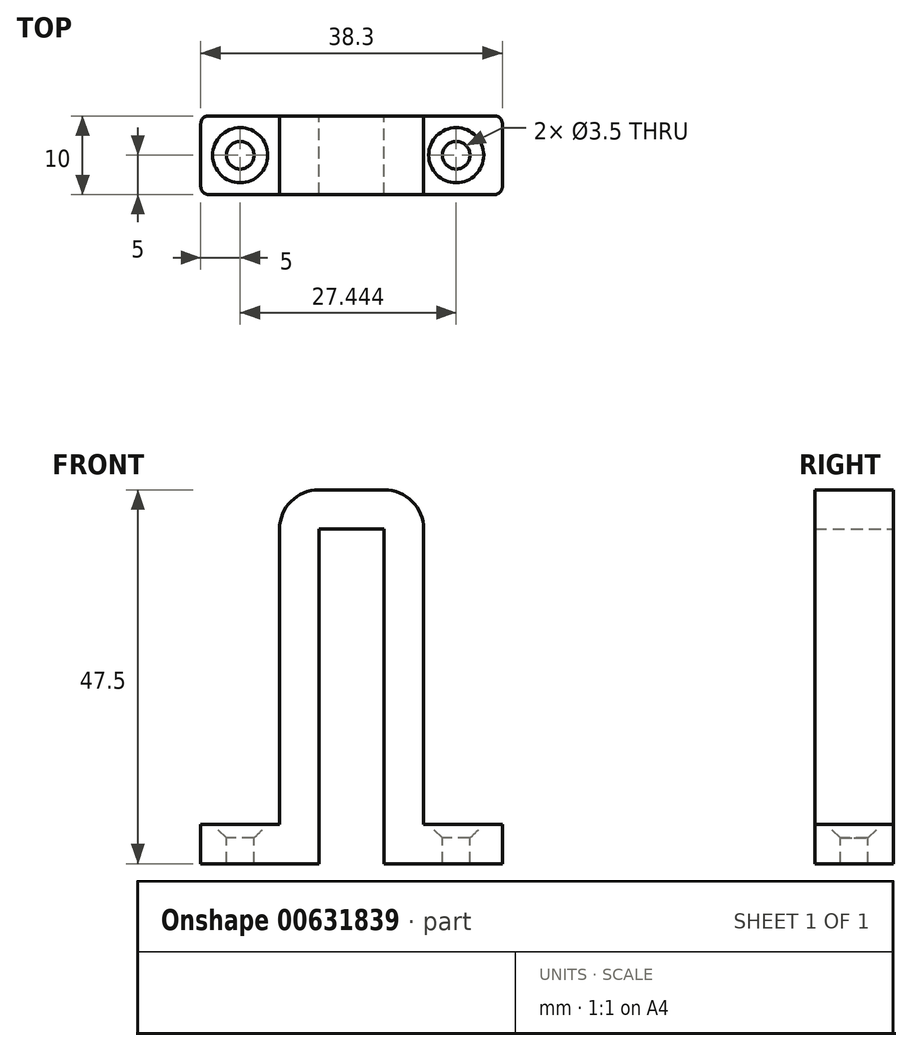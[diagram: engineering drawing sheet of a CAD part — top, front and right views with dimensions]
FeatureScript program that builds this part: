
annotation { "Feature Type Name" : "Feature", "Feature Type Description" : "" }
export const myFeature = defineFeature(function(context is Context, id is Id, definition is map)
    precondition{}
    {
        {
            var Q0;
            Q0=qCreatedBy(makeId("Front.planeOp"),FACE);
            var sketch = newSketch(context, id + "F0", { "sketchPlane" : qUnion([Q0])});
            skLineSegment(sketch, "E0", {"start": v(0, 75.6) * mm, "end": v(0, -82.63) * mm, "construction": true});
            skLineSegment(sketch, "E1", {"start": v(0, 12.13) * mm, "end": v(-4.15, 12.13) * mm});
            skLineSegment(sketch, "E2", {"start": v(-4.15, 12.13) * mm, "end": v(-4.15, -30.37) * mm});
            skLineSegment(sketch, "E3", {"start": v(-4.15, -30.37) * mm, "end": v(-19.15, -30.37) * mm});
            skLineSegment(sketch, "E4", {"start": v(-19.15, -30.37) * mm, "end": v(-19.15, -25.37) * mm});
            skLineSegment(sketch, "E5", {"start": v(-19.15, -25.37) * mm, "end": v(-9.15, -25.37) * mm});
            skLineSegment(sketch, "E6", {"start": v(-9.15, -25.37) * mm, "end": v(-9.15, 17.13) * mm});
            skLineSegment(sketch, "E7", {"start": v(-9.15, 17.13) * mm, "end": v(0, 17.13) * mm});
            skLineSegment(sketch, "E8.MirrorCS", {"start": v(0, 12.13) * mm, "end": v(4.15, 12.13) * mm});
            skLineSegment(sketch, "E9.MirrorCS", {"start": v(4.15, 12.13) * mm, "end": v(4.15, -30.37) * mm});
            skLineSegment(sketch, "E10.MirrorCS", {"start": v(4.15, -30.37) * mm, "end": v(19.15, -30.37) * mm});
            skLineSegment(sketch, "E11.MirrorCS", {"start": v(19.15, -30.37) * mm, "end": v(19.15, -25.37) * mm});
            skLineSegment(sketch, "E12.MirrorCS", {"start": v(19.15, -25.37) * mm, "end": v(9.15, -25.37) * mm});
            skLineSegment(sketch, "E13.MirrorCS", {"start": v(9.15, 17.13) * mm, "end": v(0, 17.13) * mm});
            skLineSegment(sketch, "E14.MirrorCS", {"start": v(9.15, -25.37) * mm, "end": v(9.15, 17.13) * mm});
            skSolve(sketch);
        }
        {
            var Q0;
            Q0 = qSketchRegion(id + "F0", true);
            extrude(context, id + "F1", {"entities" : qUnion([Q0]), "endBound" : BoundingType.SYMMETRIC, "depth" : 10 * mm, "offsetDistance" : 25 * mm});
        }
        {
            var Q0;
            Q0=makeQuery(id+"F1.opExtrude","SWEPT_FACE",FACE,{"disambiguationData":[OSD([sQuery(id+"F0.wireOp",EDGE,"E5")])]});
            var sketch = newSketch(context, id + "F2", { "sketchPlane" : qUnion([Q0])});
            skLineSegment(sketch, "E15", {"start": v(-19.15, 5) * mm, "end": v(-9.15, -5) * mm, "construction": true});
            skLineSegment(sketch, "E16", {"start": v(9.34, -4.85) * mm, "end": v(17.33, 4.95) * mm, "construction": true});
            skCircle(sketch, "E17", {"center": v(-14.15, 0) * mm, "radius": 1.75 * mm});
            skCircle(sketch, "E18", {"center": v(13.3, 0) * mm, "radius": 1.75 * mm});
            skSolve(sketch);
        }
        {
            var Q0;
            Q0=sQuery(id+"F2.wireOp",VERTEX,"E18.center");
            var Q1;
            Q1=makeQuery(id+"F1.opExtrude","SWEPT_BODY",BODY,{"disambiguationData":[OSD([sQuery(id+"F0.wireOp",EDGE,"E1"),sQuery(id+"F0.wireOp",EDGE,"E2"),sQuery(id+"F0.wireOp",EDGE,"E3"),sQuery(id+"F0.wireOp",EDGE,"E4"),sQuery(id+"F0.wireOp",EDGE,"E5"),sQuery(id+"F0.wireOp",EDGE,"E6"),sQuery(id+"F0.wireOp",EDGE,"E7"),sQuery(id+"F0.wireOp",EDGE,"E8.MirrorCS"),sQuery(id+"F0.wireOp",EDGE,"E9.MirrorCS"),sQuery(id+"F0.wireOp",EDGE,"E10.MirrorCS"),sQuery(id+"F0.wireOp",EDGE,"E11.MirrorCS"),sQuery(id+"F0.wireOp",EDGE,"E12.MirrorCS"),sQuery(id+"F0.wireOp",EDGE,"E13.MirrorCS"),sQuery(id+"F0.wireOp",EDGE,"E14.MirrorCS")])]});
            hole(context, id + "F3", {"style" : HoleStyle.C_SINK, "endStyle" : HoleEndStyle.THROUGH, "holeDiameter" : 3.5 * mm, "cSinkDiameter" : 7 * mm, "cSinkAngle" : 90 * degree, "majorDiameter" : 5 * mm, "isTappedThrough" : true, "tappedDepth" : 12 * mm, "tapClearance" : 3, "startFromSketch" : true, "locations" : qUnion([Q0]), "scope" : qUnion([Q1])});
        }
        {
            var Q0;
            Q0=sQuery(id+"F2.wireOp",VERTEX,"E17.center");
            var Q1;
            Q1=makeQuery(id+"F1.opExtrude","SWEPT_BODY",BODY,{"disambiguationData":[OSD([sQuery(id+"F0.wireOp",EDGE,"E1"),sQuery(id+"F0.wireOp",EDGE,"E2"),sQuery(id+"F0.wireOp",EDGE,"E3"),sQuery(id+"F0.wireOp",EDGE,"E4"),sQuery(id+"F0.wireOp",EDGE,"E5"),sQuery(id+"F0.wireOp",EDGE,"E6"),sQuery(id+"F0.wireOp",EDGE,"E7"),sQuery(id+"F0.wireOp",EDGE,"E8.MirrorCS"),sQuery(id+"F0.wireOp",EDGE,"E9.MirrorCS"),sQuery(id+"F0.wireOp",EDGE,"E10.MirrorCS"),sQuery(id+"F0.wireOp",EDGE,"E11.MirrorCS"),sQuery(id+"F0.wireOp",EDGE,"E12.MirrorCS"),sQuery(id+"F0.wireOp",EDGE,"E13.MirrorCS"),sQuery(id+"F0.wireOp",EDGE,"E14.MirrorCS")])]});
            hole(context, id + "F4", {"style" : HoleStyle.C_SINK, "endStyle" : HoleEndStyle.THROUGH, "holeDiameter" : 3.5 * mm, "cSinkDiameter" : 7 * mm, "cSinkAngle" : 90 * degree, "majorDiameter" : 5 * mm, "isTappedThrough" : true, "tappedDepth" : 12 * mm, "tapClearance" : 3, "startFromSketch" : true, "locations" : qUnion([Q0]), "scope" : qUnion([Q1])});
        }
        {
            var Q0;
            Q0=makeQuery(id+"F1.opExtrude","SWEPT_EDGE",EDGE,{"disambiguationData":[OSD([sQuery(id+"F0.wireOp",EDGE,"E6"),sQuery(id+"F0.wireOp",EDGE,"E7")])]});
            var Q1;
            Q1=makeQuery(id+"F1.opExtrude","SWEPT_EDGE",EDGE,{"disambiguationData":[OSD([sQuery(id+"F0.wireOp",EDGE,"E13.MirrorCS"),sQuery(id+"F0.wireOp",EDGE,"E14.MirrorCS")])]});
            fillet(context, id + "F5", {"entities" : qUnion([Q0, Q1]), "radius" : 5 * mm, "tangentPropagation" : true, "allowEdgeOverflow" : false});
        }
        {
            var Q0;
            Q0=makeQuery(id+"F1.opExtrude","CAP_EDGE",EDGE,{"disambiguationData":[OSD([sQuery(id+"F0.wireOp",EDGE,"E11.MirrorCS")])],"isStart":true});
            var Q1;
            Q1=makeQuery(id+"F1.opExtrude","CAP_EDGE",EDGE,{"disambiguationData":[OSD([sQuery(id+"F0.wireOp",EDGE,"E11.MirrorCS")])],"isStart":false});
            var Q2;
            Q2=makeQuery(id+"F1.opExtrude","CAP_EDGE",EDGE,{"disambiguationData":[OSD([sQuery(id+"F0.wireOp",EDGE,"E4")])],"isStart":false});
            var Q3;
            Q3=makeQuery(id+"F1.opExtrude","CAP_EDGE",EDGE,{"disambiguationData":[OSD([sQuery(id+"F0.wireOp",EDGE,"E4")])],"isStart":true});
            fillet(context, id + "F6", {"entities" : qUnion([Q0, Q1, Q2, Q3]), "radius" : 1 * mm, "tangentPropagation" : true, "allowEdgeOverflow" : false});
        }
    });
